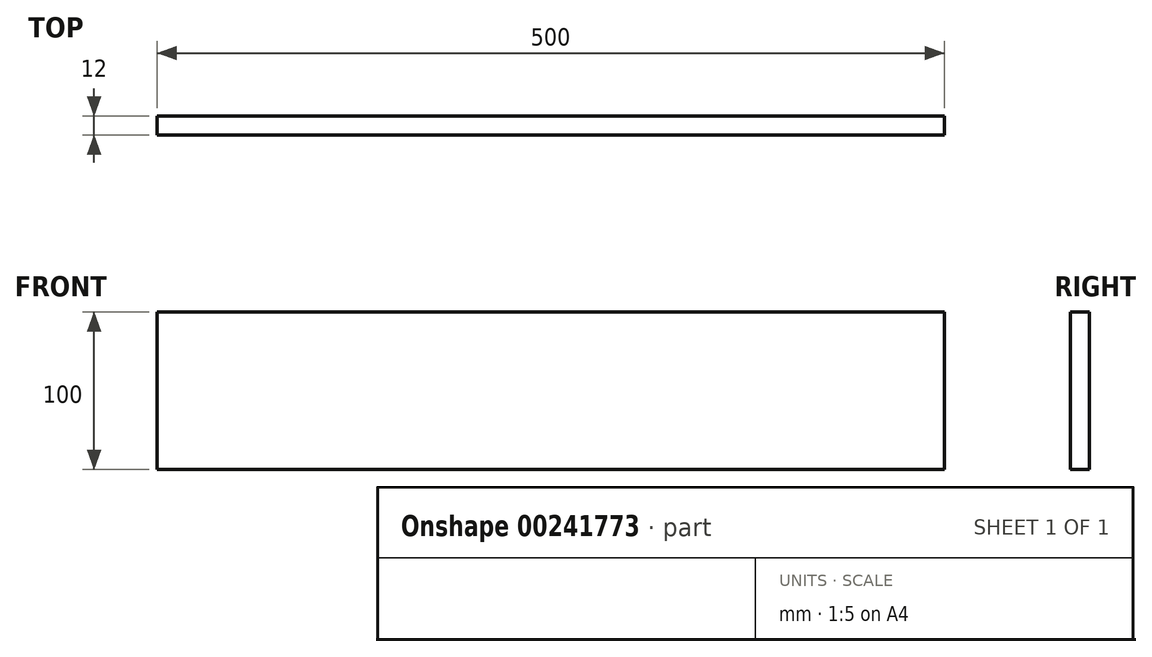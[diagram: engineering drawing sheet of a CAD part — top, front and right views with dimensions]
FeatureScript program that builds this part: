
annotation { "Feature Type Name" : "Feature", "Feature Type Description" : "" }
export const myFeature = defineFeature(function(context is Context, id is Id, definition is map)
    precondition{}
    {
        {
            var Q0;
            Q0=qCreatedBy(makeId("Front.planeOp"),FACE);
            var sketch = newSketch(context, id + "F0", { "sketchPlane" : qUnion([Q0])});
            skLineSegment(sketch, "E0.bottom", {"start": v(0, 0) * mm, "end": v(500, 0) * mm});
            skLineSegment(sketch, "E0.top", {"start": v(0, 100) * mm, "end": v(500, 100) * mm});
            skLineSegment(sketch, "E0.left", {"start": v(0, 0) * mm, "end": v(0, 100) * mm});
            skLineSegment(sketch, "E0.right", {"start": v(500, 0) * mm, "end": v(500, 100) * mm});
            skSolve(sketch);
        }
        {
            var Q0;
            Q0=qSketchRegion(id+"F0",true);
            extrude(context, id + "F1", {"entities" : qUnion([Q0]), "depth" : 12 * mm});
        }
    });
